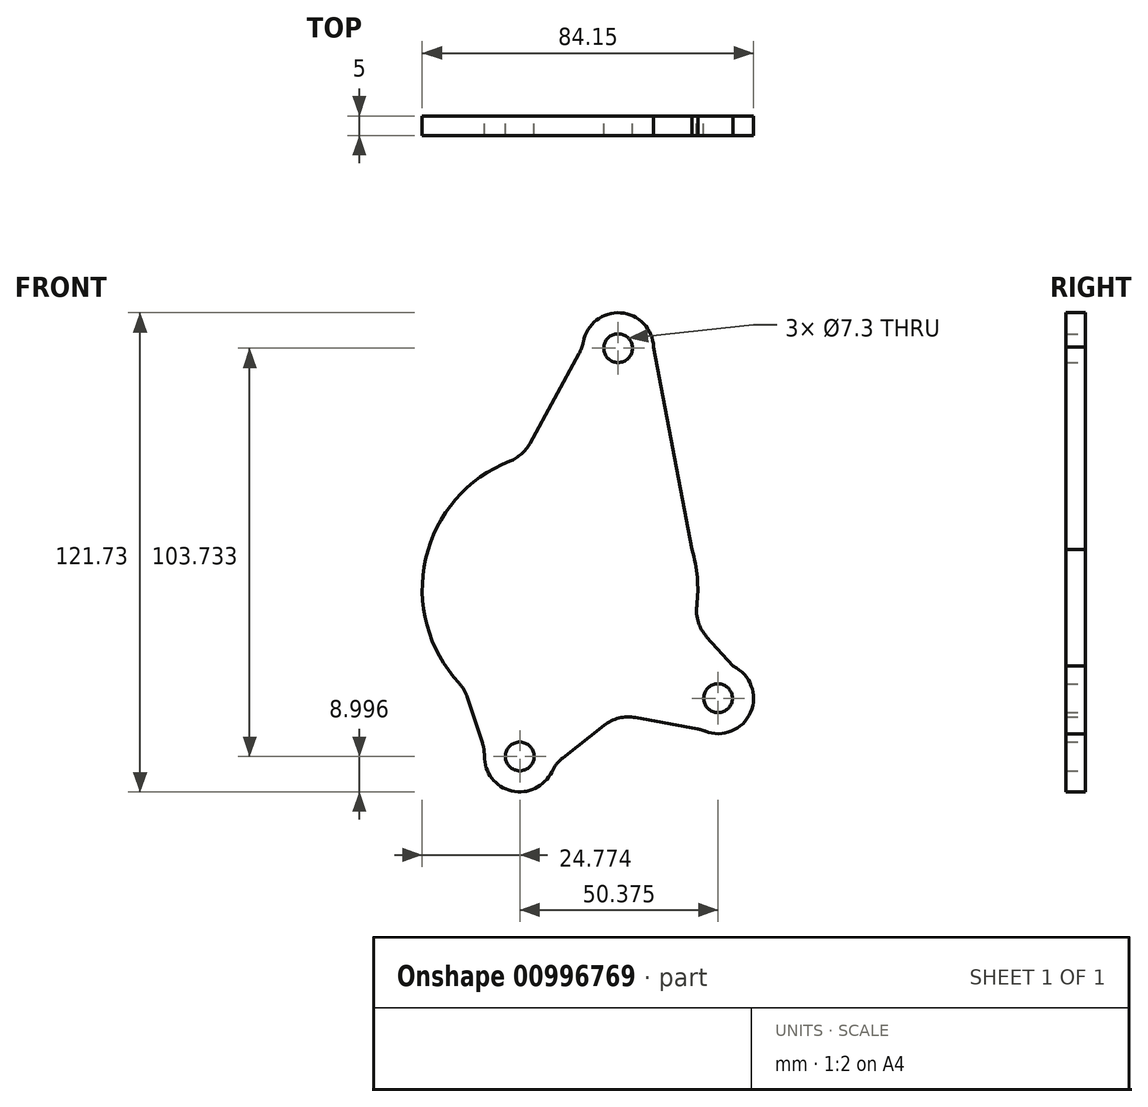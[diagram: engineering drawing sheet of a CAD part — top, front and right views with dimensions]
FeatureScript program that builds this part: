
annotation { "Feature Type Name" : "Feature", "Feature Type Description" : "" }
export const myFeature = defineFeature(function(context is Context, id is Id, definition is map)
    precondition{}
    {
        {
            var Q0;
            Q0=qCreatedBy(makeId("Front.planeOp"),FACE);
            var sketch = newSketch(context, id + "F0", { "sketchPlane" : qUnion([Q0])});
            skCircle(sketch, "E0", {"center": v(-24.99, -78.7) * mm, "radius": 3.65 * mm});
            skCircle(sketch, "E1", {"center": v(25.39, -63.92) * mm, "radius": 3.65 * mm});
            skCircle(sketch, "E2", {"center": v(0, 25.03) * mm, "radius": 3.65 * mm});
            skArc(sketch, "E3", {"start": v(9, 25.34) * mm, "mid": v(0.66, 34) * mm, "end": v(-8.85, 26.65) * mm});
            skArc(sketch, "E4", {"start": v(22.05, -72.28) * mm, "mid": v(33.65, -67.5) * mm, "end": v(29.2, -55.77) * mm});
            skArc(sketch, "E5", {"start": v(-33.98, -78.57) * mm, "mid": v(-27.04, -87.47) * mm, "end": v(-16.86, -82.58) * mm});
            skArc(sketch, "E6", {"start": v(-27.53, -3.68) * mm, "mid": v(-48.88, -28.47) * mm, "end": v(-40.42, -60.07) * mm});
            skLineSegment(sketch, "E7", {"start": v(29.2, -55.77) * mm, "end": v(22.48, -48.28) * mm});
            skLineSegment(sketch, "E8", {"start": v(20.16, -71.73) * mm, "end": v(4.44, -68.82) * mm});
            skLineSegment(sketch, "E9", {"start": v(-3.55, -70.8) * mm, "end": v(-14.01, -79.02) * mm});
            skLineSegment(sketch, "E10", {"start": v(-34.48, -75.32) * mm, "end": v(-38.24, -63.77) * mm});
            skLineSegment(sketch, "E11", {"start": v(9, 25.34) * mm, "end": v(18.74, -26.14) * mm});
            skLineSegment(sketch, "E12", {"start": v(-9.92, 23.65) * mm, "end": v(-22.4, 0.83) * mm});
            skArc(sketch, "E13.trimOffspring", {"start": v(19.99, -40.41) * mm, "mid": v(20.1, -33.21) * mm, "end": v(18.74, -26.14) * mm});
            skPoint(sketch, "E14.visualSharp", {"position": v(-24.28, -2.59) * mm});
            skArc(sketch, "E14.filletArc", {"start": v(-27.53, -3.68) * mm, "mid": v(-24.57, -1.88) * mm, "end": v(-22.4, 0.83) * mm});
            skPoint(sketch, "E15.visualSharp", {"position": v(19.22, -44.65) * mm});
            skArc(sketch, "E15.filletArc", {"start": v(19.99, -40.41) * mm, "mid": v(20.39, -44.61) * mm, "end": v(22.48, -48.28) * mm});
            skPoint(sketch, "E16.visualSharp", {"position": v(0, -68) * mm});
            skArc(sketch, "E16.filletArc", {"start": v(4.44, -68.82) * mm, "mid": v(0.23, -68.95) * mm, "end": v(-3.55, -70.8) * mm});
            skPoint(sketch, "E17.visualSharp", {"position": v(-38.97, -61.55) * mm});
            skArc(sketch, "E17.filletArc", {"start": v(-38.24, -63.77) * mm, "mid": v(-39.13, -61.8) * mm, "end": v(-40.42, -60.07) * mm});
            skPoint(sketch, "E18.visualSharp", {"position": v(-33.86, -77.21) * mm});
            skArc(sketch, "E18.filletArc", {"start": v(-33.98, -78.57) * mm, "mid": v(-34.1, -76.93) * mm, "end": v(-34.48, -75.32) * mm});
            skPoint(sketch, "E19.visualSharp", {"position": v(-16.22, -80.75) * mm});
            skArc(sketch, "E19.filletArc", {"start": v(-14.01, -79.02) * mm, "mid": v(-15.64, -80.63) * mm, "end": v(-16.86, -82.58) * mm});
            skPoint(sketch, "E20.visualSharp", {"position": v(-9, 25.34) * mm});
            skArc(sketch, "E20.filletArc", {"start": v(-9.92, 23.65) * mm, "mid": v(-9.26, 25.1) * mm, "end": v(-8.85, 26.65) * mm});
            skPoint(sketch, "E21.visualSharp", {"position": v(21.31, -71.94) * mm});
            skArc(sketch, "E21.filletArc", {"start": v(22.05, -72.28) * mm, "mid": v(21.12, -71.96) * mm, "end": v(20.16, -71.73) * mm});
            skSolve(sketch);
        }
        {
            var Q0;
            Q0=makeQuery(id+"F0.imprint","IMPRINT",FACE,{"disambiguationData":[TD([[makeQuery(id+"F0.imprint","IMPRINT",EDGE,{"derivedFrom":sQuery(id+"F0.wireOp",EDGE,"E0")}),-1.0]])]});
            extrude(context, id + "F1", {"entities" : qUnion([Q0]), "depth" : 5 * mm, "offsetDistance" : 25 * mm});
        }
    });
